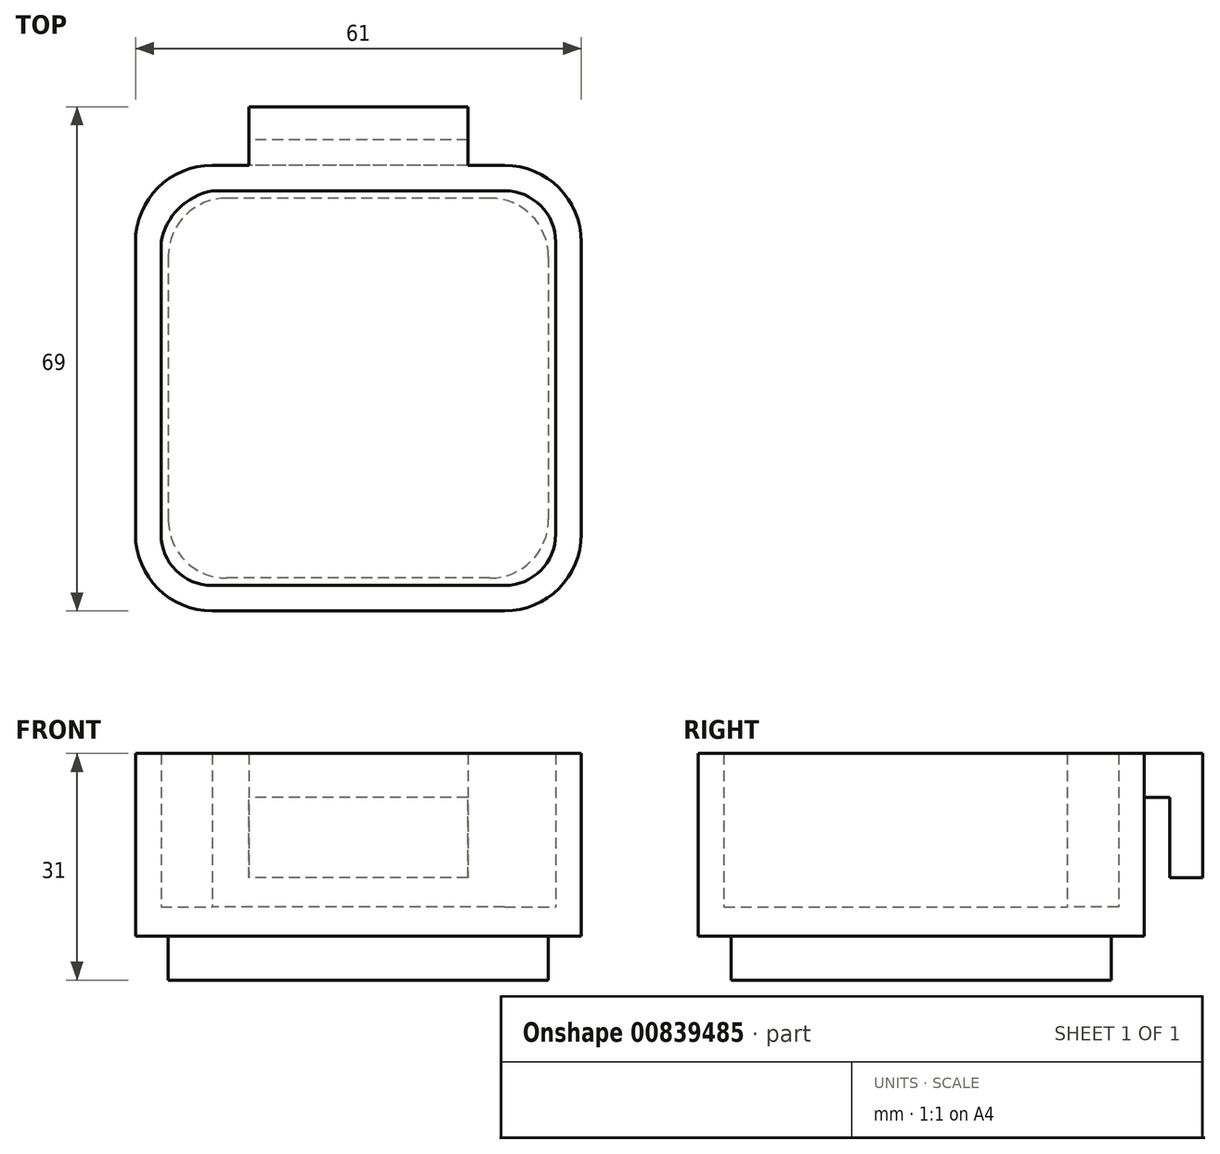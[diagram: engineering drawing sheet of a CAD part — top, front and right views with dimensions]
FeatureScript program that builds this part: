
annotation { "Feature Type Name" : "Feature", "Feature Type Description" : "" }
export const myFeature = defineFeature(function(context is Context, id is Id, definition is map)
    precondition{}
    {
        {
            var Q0;
            Q0=qCreatedBy(makeId("Top.planeOp"),FACE);
            var sketch = newSketch(context, id + "F0", { "sketchPlane" : qUnion([Q0])});
            skLineSegment(sketch, "E0.bottom", {"start": v(30.5, -30.5) * mm, "end": v(-30.5, -30.5) * mm});
            skLineSegment(sketch, "E0.top", {"start": v(30.5, 30.5) * mm, "end": v(-30.5, 30.5) * mm});
            skLineSegment(sketch, "E0.left", {"start": v(30.5, -30.5) * mm, "end": v(30.5, 30.5) * mm});
            skLineSegment(sketch, "E0.right", {"start": v(-30.5, -30.5) * mm, "end": v(-30.5, 30.5) * mm});
            skPoint(sketch, "E0.middle", {"position": v(0, 0) * mm});
            skLineSegment(sketch, "E1.bottom", {"start": v(30.5, -20) * mm, "end": v(-30.5, -20) * mm});
            skLineSegment(sketch, "E1.top", {"start": v(30.5, 20) * mm, "end": v(-30.5, 20) * mm});
            skLineSegment(sketch, "E1.left", {"start": v(30.5, -20) * mm, "end": v(30.5, 20) * mm});
            skLineSegment(sketch, "E1.right", {"start": v(-30.5, -20) * mm, "end": v(-30.5, 20) * mm});
            skLineSegment(sketch, "E2.bottom", {"start": v(20, -30.5) * mm, "end": v(-20, -30.5) * mm});
            skLineSegment(sketch, "E2.top", {"start": v(20, 30.5) * mm, "end": v(-20, 30.5) * mm});
            skLineSegment(sketch, "E2.left", {"start": v(20, -30.5) * mm, "end": v(20, 30.5) * mm});
            skLineSegment(sketch, "E2.right", {"start": v(-20, -30.5) * mm, "end": v(-20, 30.5) * mm});
            skArc(sketch, "E3", {"start": v(-20, 30.5) * mm, "mid": v(-27.42, 27.42) * mm, "end": v(-30.5, 20) * mm});
            skArc(sketch, "E4", {"start": v(30.5, 20) * mm, "mid": v(27.42, 27.42) * mm, "end": v(20, 30.5) * mm});
            skArc(sketch, "E5", {"start": v(20, -30.5) * mm, "mid": v(27.42, -27.42) * mm, "end": v(30.5, -20) * mm});
            skArc(sketch, "E6", {"start": v(-30.5, -20) * mm, "mid": v(-27.42, -27.42) * mm, "end": v(-20, -30.5) * mm});
            skLineSegment(sketch, "E7.bottom", {"start": v(27, -27) * mm, "end": v(-27, -27) * mm});
            skLineSegment(sketch, "E7.top", {"start": v(27, 27) * mm, "end": v(-27, 27) * mm});
            skLineSegment(sketch, "E7.left", {"start": v(27, -27) * mm, "end": v(27, 27) * mm});
            skLineSegment(sketch, "E7.right", {"start": v(-27, -27) * mm, "end": v(-27, 27) * mm});
            skLineSegment(sketch, "E8.bottom", {"start": v(27, 20) * mm, "end": v(-27, 20) * mm});
            skLineSegment(sketch, "E8.top", {"start": v(27, -20) * mm, "end": v(-27, -20) * mm});
            skLineSegment(sketch, "E8.left", {"start": v(27, 20) * mm, "end": v(27, -20) * mm});
            skLineSegment(sketch, "E8.right", {"start": v(-27, 20) * mm, "end": v(-27, -20) * mm});
            skLineSegment(sketch, "E9.bottom", {"start": v(20, -27) * mm, "end": v(-20, -27) * mm});
            skLineSegment(sketch, "E9.top", {"start": v(20, 27) * mm, "end": v(-20, 27) * mm});
            skLineSegment(sketch, "E9.left", {"start": v(20, -27) * mm, "end": v(20, 27) * mm});
            skLineSegment(sketch, "E9.right", {"start": v(-20, -27) * mm, "end": v(-20, 27) * mm});
            skArc(sketch, "E10", {"start": v(-20, 27) * mm, "mid": v(-24.58, 24.58) * mm, "end": v(-27, 20) * mm});
            skArc(sketch, "E11", {"start": v(27, 20) * mm, "mid": v(24.95, 24.95) * mm, "end": v(20, 27) * mm});
            skArc(sketch, "E12", {"start": v(20, -27) * mm, "mid": v(24.95, -24.95) * mm, "end": v(27, -20) * mm});
            skArc(sketch, "E13", {"start": v(-27, -20) * mm, "mid": v(-24.95, -24.95) * mm, "end": v(-20, -27) * mm});
            skSolve(sketch);
        }
        {
            var Q0;
            {var subQ0=sQuery(id+"F0.wireOp",EDGE,"E2.right");var subQ1=sQuery(id+"F0.wireOp",EDGE,"E1.bottom");var subQ2=makeQuery(id+"F0.imprint","INTERSECT",VERTEX,{"derivedFrom":[subQ1,subQ0]});Q0=makeQuery(id+"F0.imprint","IMPRINT",FACE,{"disambiguationData":[TD([[makeQuery(id+"F0.imprint","IMPRINT",EDGE,{"disambiguationData":[TD([[subQ2,-1.0]])],"derivedFrom":subQ0}),1.0]])]});}
            var Q1;
            {var subQ0=sQuery(id+"F0.wireOp",EDGE,"E10");Q1=makeQuery(id+"F0.imprint","IMPRINT",FACE,{"disambiguationData":[TD([[makeQuery(id+"F0.imprint","IMPRINT",EDGE,{"derivedFrom":subQ0}),1.0]])]});}
            var Q2;
            {var subQ0=sQuery(id+"F0.wireOp",EDGE,"E2.left");var subQ1=sQuery(id+"F0.wireOp",EDGE,"E1.top");var subQ2=makeQuery(id+"F0.imprint","INTERSECT",VERTEX,{"derivedFrom":[subQ1,subQ0]});Q2=makeQuery(id+"F0.imprint","IMPRINT",FACE,{"disambiguationData":[TD([[makeQuery(id+"F0.imprint","IMPRINT",EDGE,{"disambiguationData":[TD([[subQ2,-1.0]])],"derivedFrom":subQ1}),-1.0]])]});}
            var Q3;
            {var subQ0=sQuery(id+"F0.wireOp",EDGE,"E2.left");var subQ1=sQuery(id+"F0.wireOp",EDGE,"E1.bottom");var subQ2=makeQuery(id+"F0.imprint","INTERSECT",VERTEX,{"derivedFrom":[subQ1,subQ0]});Q3=makeQuery(id+"F0.imprint","IMPRINT",FACE,{"disambiguationData":[TD([[makeQuery(id+"F0.imprint","IMPRINT",EDGE,{"disambiguationData":[TD([[subQ2,-1.0]])],"derivedFrom":subQ1}),-1.0]])]});}
            var Q4;
            {var subQ3=sQuery(id+"F0.wireOp",EDGE,"E11");Q4=makeQuery(id+"F0.imprint","IMPRINT",FACE,{"disambiguationData":[TD([[makeQuery(id+"F0.imprint","IMPRINT",EDGE,{"derivedFrom":subQ3}),1.0]])]});}
            var Q5;
            {var subQ0=sQuery(id+"F0.wireOp",EDGE,"E2.left");var subQ1=sQuery(id+"F0.wireOp",EDGE,"E1.bottom");var subQ2=makeQuery(id+"F0.imprint","INTERSECT",VERTEX,{"derivedFrom":[subQ1,subQ0]});Q5=makeQuery(id+"F0.imprint","IMPRINT",FACE,{"disambiguationData":[TD([[makeQuery(id+"F0.imprint","IMPRINT",EDGE,{"disambiguationData":[TD([[subQ2,-1.0]])],"derivedFrom":subQ0}),-1.0]])]});}
            var Q6;
            {var subQ0=sQuery(id+"F0.wireOp",EDGE,"E2.left");var subQ1=sQuery(id+"F0.wireOp",EDGE,"E1.bottom");var subQ2=makeQuery(id+"F0.imprint","INTERSECT",VERTEX,{"derivedFrom":[subQ1,subQ0]});Q6=makeQuery(id+"F0.imprint","IMPRINT",FACE,{"disambiguationData":[TD([[makeQuery(id+"F0.imprint","IMPRINT",EDGE,{"disambiguationData":[TD([[subQ2,-1.0]])],"derivedFrom":subQ1}),1.0]])]});}
            var Q7;
            {var subQ3=sQuery(id+"F0.wireOp",EDGE,"E12");Q7=makeQuery(id+"F0.imprint","IMPRINT",FACE,{"disambiguationData":[TD([[makeQuery(id+"F0.imprint","IMPRINT",EDGE,{"derivedFrom":subQ3}),1.0]])]});}
            var Q8;
            {var subQ3=sQuery(id+"F0.wireOp",EDGE,"E13");Q8=makeQuery(id+"F0.imprint","IMPRINT",FACE,{"disambiguationData":[TD([[makeQuery(id+"F0.imprint","IMPRINT",EDGE,{"derivedFrom":subQ3}),1.0]])]});}
            extrude(context, id + "F1", {"entities" : qUnion([Q0, Q1, Q2, Q3, Q4, Q5, Q6, Q7, Q8]), "depth" : 4 * mm, "offsetDistance" : 25 * mm});
        }
        {
            var Q0;
            {var subQ6=sQuery(id+"F0.wireOp",EDGE,"E5");Q0=makeQuery(id+"F0.imprint","IMPRINT",FACE,{"disambiguationData":[TD([[makeQuery(id+"F0.imprint","IMPRINT",EDGE,{"derivedFrom":subQ6}),1.0]])]});}
            var Q1;
            {var subQ0=sQuery(id+"F0.wireOp",EDGE,"E12");Q1=makeQuery(id+"F0.imprint","IMPRINT",FACE,{"disambiguationData":[TD([[makeQuery(id+"F0.imprint","IMPRINT",EDGE,{"derivedFrom":subQ0}),-1.0]])]});}
            var Q2;
            {var subQ0=sQuery(id+"F0.wireOp",EDGE,"E2.left");var subQ1=sQuery(id+"F0.wireOp",EDGE,"E0.bottom");var subQ2=makeQuery(id+"F0.imprint","INTERSECT",VERTEX,{"derivedFrom":[subQ1,subQ0,sQuery(id+"F0.wireOp",EDGE,"E5")]});Q2=makeQuery(id+"F0.imprint","IMPRINT",FACE,{"disambiguationData":[TD([[makeQuery(id+"F0.imprint","IMPRINT",EDGE,{"disambiguationData":[TD([[subQ2,-1.0]])],"derivedFrom":subQ1}),-1.0]])]});}
            var Q3;
            {var subQ6=sQuery(id+"F0.wireOp",EDGE,"E6");Q3=makeQuery(id+"F0.imprint","IMPRINT",FACE,{"disambiguationData":[TD([[makeQuery(id+"F0.imprint","IMPRINT",EDGE,{"derivedFrom":subQ6}),1.0]])]});}
            var Q4;
            {var subQ0=sQuery(id+"F0.wireOp",EDGE,"E13");Q4=makeQuery(id+"F0.imprint","IMPRINT",FACE,{"disambiguationData":[TD([[makeQuery(id+"F0.imprint","IMPRINT",EDGE,{"derivedFrom":subQ0}),-1.0]])]});}
            var Q5;
            {var subQ0=sQuery(id+"F0.wireOp",EDGE,"E1.bottom");var subQ1=sQuery(id+"F0.wireOp",EDGE,"E0.right");var subQ2=makeQuery(id+"F0.imprint","INTERSECT",VERTEX,{"derivedFrom":[subQ1,subQ0,sQuery(id+"F0.wireOp",EDGE,"E6")]});Q5=makeQuery(id+"F0.imprint","IMPRINT",FACE,{"disambiguationData":[TD([[makeQuery(id+"F0.imprint","IMPRINT",EDGE,{"disambiguationData":[TD([[subQ2,-1.0]])],"derivedFrom":subQ1}),-1.0]])]});}
            var Q6;
            {var subQ6=sQuery(id+"F0.wireOp",EDGE,"E3");Q6=makeQuery(id+"F0.imprint","IMPRINT",FACE,{"disambiguationData":[TD([[makeQuery(id+"F0.imprint","IMPRINT",EDGE,{"derivedFrom":subQ6}),1.0]])]});}
            var Q7;
            {var subQ3=sQuery(id+"F0.wireOp",EDGE,"E10");Q7=makeQuery(id+"F0.imprint","IMPRINT",FACE,{"disambiguationData":[TD([[makeQuery(id+"F0.imprint","IMPRINT",EDGE,{"derivedFrom":subQ3}),-1.0]])]});}
            var Q8;
            {var subQ0=sQuery(id+"F0.wireOp",EDGE,"E2.left");var subQ1=sQuery(id+"F0.wireOp",EDGE,"E0.top");var subQ2=makeQuery(id+"F0.imprint","INTERSECT",VERTEX,{"derivedFrom":[subQ1,subQ0,sQuery(id+"F0.wireOp",EDGE,"E4")]});Q8=makeQuery(id+"F0.imprint","IMPRINT",FACE,{"disambiguationData":[TD([[makeQuery(id+"F0.imprint","IMPRINT",EDGE,{"disambiguationData":[TD([[subQ2,-1.0]])],"derivedFrom":subQ1}),1.0]])]});}
            var Q9;
            {var subQ0=sQuery(id+"F0.wireOp",EDGE,"E4");Q9=makeQuery(id+"F0.imprint","IMPRINT",FACE,{"disambiguationData":[TD([[makeQuery(id+"F0.imprint","IMPRINT",EDGE,{"derivedFrom":subQ0}),1.0]])]});}
            var Q10;
            {var subQ0=sQuery(id+"F0.wireOp",EDGE,"E11");Q10=makeQuery(id+"F0.imprint","IMPRINT",FACE,{"disambiguationData":[TD([[makeQuery(id+"F0.imprint","IMPRINT",EDGE,{"derivedFrom":subQ0}),-1.0]])]});}
            var Q11;
            {var subQ0=sQuery(id+"F0.wireOp",EDGE,"E1.bottom");var subQ1=sQuery(id+"F0.wireOp",EDGE,"E0.left");var subQ2=makeQuery(id+"F0.imprint","INTERSECT",VERTEX,{"derivedFrom":[subQ1,subQ0,sQuery(id+"F0.wireOp",EDGE,"E5")]});Q11=makeQuery(id+"F0.imprint","IMPRINT",FACE,{"disambiguationData":[TD([[makeQuery(id+"F0.imprint","IMPRINT",EDGE,{"disambiguationData":[TD([[subQ2,-1.0]])],"derivedFrom":subQ1}),1.0]])]});}
            extrude(context, id + "F2", {"entities" : qUnion([Q0, Q1, Q2, Q3, Q4, Q5, Q6, Q7, Q8, Q9, Q10, Q11]), "operationType" : NewBodyOperationType.ADD, "depth" : 25 * mm, "offsetDistance" : 25 * mm});
        }
        {
            var Q0;
            Q0=makeQuery(id+"F2.opExtrude","SWEPT_FACE",FACE,{"disambiguationData":[OSD([sQuery(id+"F0.wireOp",EDGE,"E0.top")])]});
            var sketch = newSketch(context, id + "F3", { "sketchPlane" : qUnion([Q0])});
            skLineSegment(sketch, "E14.bottom", {"start": v(15, 25) * mm, "end": v(-15, 25) * mm});
            skLineSegment(sketch, "E14.top", {"start": v(15, -25) * mm, "end": v(-15, -25) * mm});
            skLineSegment(sketch, "E14.left", {"start": v(15, 25) * mm, "end": v(15, -25) * mm});
            skLineSegment(sketch, "E14.right", {"start": v(-15, 25) * mm, "end": v(-15, -25) * mm});
            skPoint(sketch, "E14.middle", {"position": v(0, 0) * mm});
            skLineSegment(sketch, "E15.bottom", {"start": v(15, 8) * mm, "end": v(-15, 8) * mm});
            skLineSegment(sketch, "E15.top", {"start": v(15, -8) * mm, "end": v(-15, -8) * mm});
            skLineSegment(sketch, "E15.left", {"start": v(15, 8) * mm, "end": v(15, -8) * mm});
            skLineSegment(sketch, "E15.right", {"start": v(-15, 8) * mm, "end": v(-15, -8) * mm});
            skSolve(sketch);
        }
        {
            var Q0;
            {var subQ0=sQuery(id+"F3.wireOp",EDGE,"E14.bottom");Q0=makeQuery(id+"F3.imprint","IMPRINT",FACE,{"disambiguationData":[TD([[makeQuery(id+"F3.imprint","IMPRINT",EDGE,{"derivedFrom":subQ0}),-1.0]])]});}
            extrude(context, id + "F4", {"entities" : qUnion([Q0]), "operationType" : NewBodyOperationType.ADD, "depth" : 8 * mm, "offsetDistance" : 25 * mm});
        }
        {
            var Q0;
            Q0=makeQuery(id+"F4.opExtrude","SWEPT_FACE",FACE,{"disambiguationData":[OSD([sQuery(id+"F3.wireOp",EDGE,"E14.left")])]});
            var sketch = newSketch(context, id + "F5", { "sketchPlane" : qUnion([Q0])});
            skLineSegment(sketch, "E16.bottom", {"start": v(-30.5, 8) * mm, "end": v(-34, 8) * mm});
            skLineSegment(sketch, "E16.top", {"start": v(-30.5, 19) * mm, "end": v(-34, 19) * mm});
            skLineSegment(sketch, "E16.left", {"start": v(-30.5, 8) * mm, "end": v(-30.5, 19) * mm});
            skLineSegment(sketch, "E16.right", {"start": v(-34, 8) * mm, "end": v(-34, 19) * mm});
            skSolve(sketch);
        }
        {
            var Q0;
            Q0=makeQuery(id+"F5.imprint","IMPRINT",FACE,{"disambiguationData":[TD([[makeQuery(id+"F5.imprint","IMPRINT",EDGE,{"derivedFrom":sQuery(id+"F5.wireOp",EDGE,"E16.bottom")}),1.0]])]});
            extrude(context, id + "F6", {"entities" : qUnion([Q0]), "operationType" : NewBodyOperationType.REMOVE, "oppositeDirection" : true, "depth" : 33 * mm, "offsetDistance" : 25 * mm});
        }
        {
            var Q0;
            {var subQ0=sQuery(id+"F0.wireOp",EDGE,"E13");var subQ1=sQuery(id+"F0.wireOp",EDGE,"E12");var subQ2=sQuery(id+"F0.wireOp",EDGE,"E11");var subQ3=sQuery(id+"F0.wireOp",EDGE,"E10");var subQ4=sQuery(id+"F0.wireOp",EDGE,"E7.right");var subQ5=sQuery(id+"F0.wireOp",EDGE,"E7.left");var subQ6=sQuery(id+"F0.wireOp",EDGE,"E7.top");var subQ7=sQuery(id+"F0.wireOp",EDGE,"E7.bottom");Q0=makeQuery(id+"F2.boolean.opBoolean","MERGE",FACE,{"derivedFrom":[makeQuery(id+"F1.opExtrude","CAP_FACE",FACE,{"disambiguationData":[OSD([subQ7,subQ6,subQ5,subQ4,subQ3,subQ2,subQ1,subQ0])],"isStart":true}),makeQuery(id+"F2.opExtrude","CAP_FACE",FACE,{"disambiguationData":[OSD([sQuery(id+"F0.wireOp",EDGE,"E0.bottom"),sQuery(id+"F0.wireOp",EDGE,"E0.top"),sQuery(id+"F0.wireOp",EDGE,"E0.left"),sQuery(id+"F0.wireOp",EDGE,"E0.right"),sQuery(id+"F0.wireOp",EDGE,"E3"),sQuery(id+"F0.wireOp",EDGE,"E4"),sQuery(id+"F0.wireOp",EDGE,"E5"),sQuery(id+"F0.wireOp",EDGE,"E6"),subQ7,subQ6,subQ5,subQ4,subQ3,subQ2,subQ1,subQ0])],"isStart":true})]});}
            var sketch = newSketch(context, id + "F7", { "sketchPlane" : qUnion([Q0])});
            skLineSegment(sketch, "E17.bottom", {"start": v(26, -26) * mm, "end": v(-26, -26) * mm});
            skLineSegment(sketch, "E17.top", {"start": v(26, 26) * mm, "end": v(-26, 26) * mm});
            skLineSegment(sketch, "E17.left", {"start": v(26, -26) * mm, "end": v(26, 26) * mm});
            skLineSegment(sketch, "E17.right", {"start": v(-26, -26) * mm, "end": v(-26, 26) * mm});
            skPoint(sketch, "E17.middle", {"position": v(0, 0) * mm});
            skSolve(sketch);
        }
        {
            var Q0;
            Q0=makeQuery(id+"F7.imprint","IMPRINT",FACE,{"disambiguationData":[TD([[makeQuery(id+"F7.imprint","IMPRINT",EDGE,{"derivedFrom":sQuery(id+"F7.wireOp",EDGE,"E17.bottom")}),-1.0]])]});
            extrude(context, id + "F8", {"entities" : qUnion([Q0]), "operationType" : NewBodyOperationType.ADD, "depth" : 6 * mm, "offsetDistance" : 25 * mm});
        }
        {
            var Q0;
            Q0=makeQuery(id+"F8.opExtrude","SWEPT_EDGE",EDGE,{"disambiguationData":[OSD([sQuery(id+"F7.wireOp",EDGE,"E17.top"),sQuery(id+"F7.wireOp",EDGE,"E17.right")])]});
            var Q1;
            Q1=makeQuery(id+"F8.opExtrude","SWEPT_EDGE",EDGE,{"disambiguationData":[OSD([sQuery(id+"F7.wireOp",EDGE,"E17.top"),sQuery(id+"F7.wireOp",EDGE,"E17.left")])]});
            var Q2;
            Q2=makeQuery(id+"F8.opExtrude","SWEPT_EDGE",EDGE,{"disambiguationData":[OSD([sQuery(id+"F7.wireOp",EDGE,"E17.bottom"),sQuery(id+"F7.wireOp",EDGE,"E17.left")])]});
            var Q3;
            Q3=makeQuery(id+"F8.opExtrude","SWEPT_EDGE",EDGE,{"disambiguationData":[OSD([sQuery(id+"F7.wireOp",EDGE,"E17.bottom"),sQuery(id+"F7.wireOp",EDGE,"E17.right")])]});
            fillet(context, id + "F9", {"entities" : qUnion([Q0, Q1, Q2, Q3]), "radius" : 8 * mm, "tangentPropagation" : true, "allowEdgeOverflow" : false});
        }
    });
